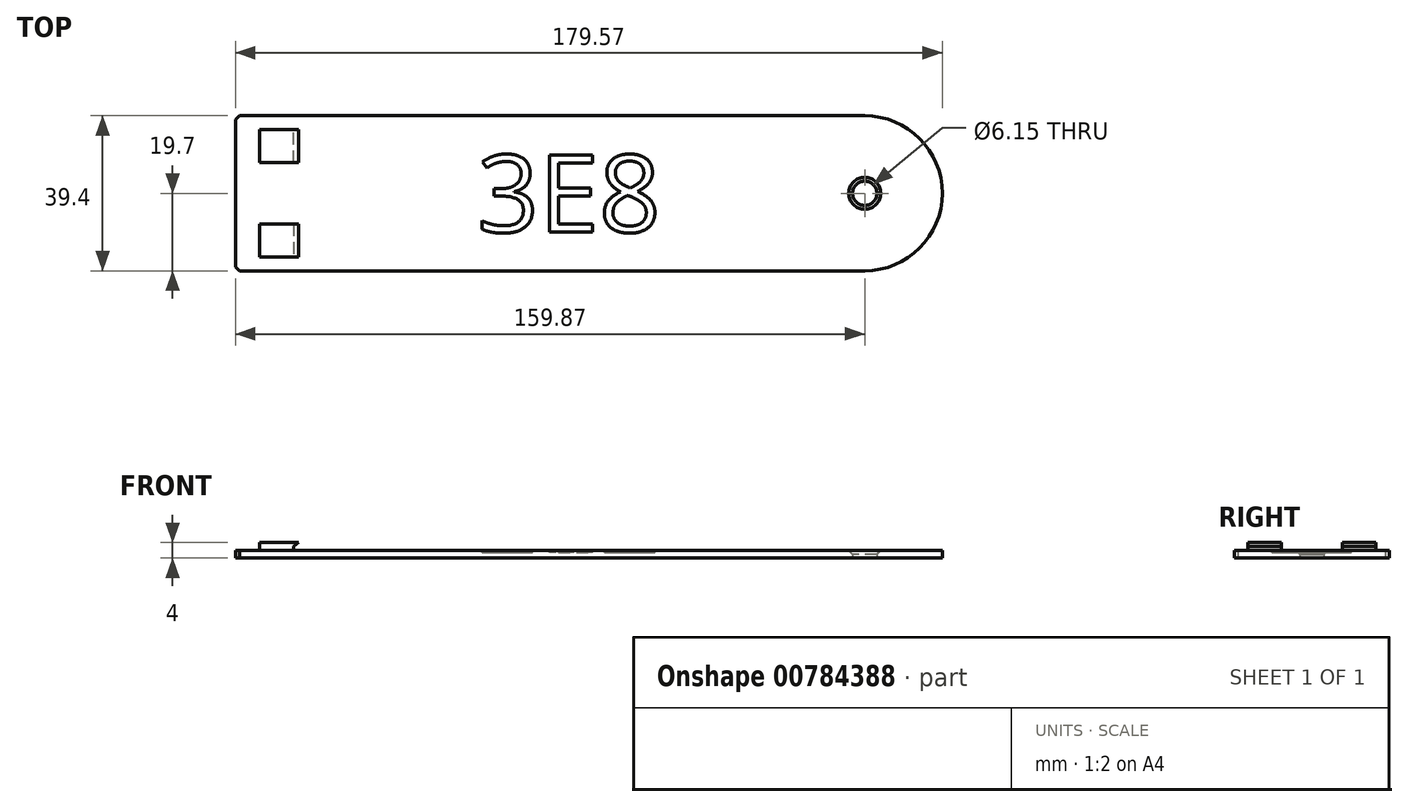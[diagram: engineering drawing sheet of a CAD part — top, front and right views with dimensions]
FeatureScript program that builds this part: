
annotation { "Feature Type Name" : "Feature", "Feature Type Description" : "" }
export const myFeature = defineFeature(function(context is Context, id is Id, definition is map)
    precondition{}
    {
        {
            assignVariable(context, id + "F0", {"name" : "slatthickness", "anyValue" : 2});
        }
        {
            var Q0;
            Q0=qCreatedBy(makeId("Top.planeOp"),FACE);
            var sketch = newSketch(context, id + "F1", { "sketchPlane" : qUnion([Q0])});
            skLineSegment(sketch, "E0", {"start": v(-75, 0) * mm, "end": v(75, 0) * mm, "construction": true});
            skLineSegment(sketch, "E1", {"start": v(-75, 12) * mm, "end": v(-75, -12) * mm, "construction": true});
            skLineSegment(sketch, "E2.bottom", {"start": v(-70.14, 7.8) * mm, "end": v(-79.86, 7.8) * mm, "construction": true});
            skLineSegment(sketch, "E2.top", {"start": v(-70.14, 16.2) * mm, "end": v(-79.86, 16.2) * mm, "construction": true});
            skLineSegment(sketch, "E2.left", {"start": v(-70.14, 7.8) * mm, "end": v(-70.14, 16.2) * mm, "construction": true});
            skLineSegment(sketch, "E2.right", {"start": v(-79.86, 7.8) * mm, "end": v(-79.86, 16.2) * mm, "construction": true});
            skPoint(sketch, "E2.middle", {"position": v(-75, 12) * mm});
            skLineSegment(sketch, "E3.MirrorCS", {"start": v(-70.14, -7.8) * mm, "end": v(-70.14, -16.2) * mm, "construction": true});
            skLineSegment(sketch, "E4.MirrorCS", {"start": v(-70.14, -16.2) * mm, "end": v(-79.86, -16.2) * mm, "construction": true});
            skLineSegment(sketch, "E5.MirrorCS", {"start": v(-79.86, -7.8) * mm, "end": v(-79.86, -16.2) * mm, "construction": true});
            skLineSegment(sketch, "E6.MirrorCS", {"start": v(-70.14, -7.8) * mm, "end": v(-79.86, -7.8) * mm, "construction": true});
            skCircle(sketch, "E7", {"center": v(75, 0) * mm, "radius": 3.08 * mm});
            skArc(sketch, "E8", {"start": v(75, -19.7) * mm, "mid": v(94.7, 0) * mm, "end": v(75, 19.7) * mm});
            skLineSegment(sketch, "E9", {"start": v(75, 19.7) * mm, "end": v(75, -19.7) * mm, "construction": true});
            skLineSegment(sketch, "E10", {"start": v(75, 19.7) * mm, "end": v(-84.87, 19.7) * mm});
            skLineSegment(sketch, "E11", {"start": v(-84.87, 19.7) * mm, "end": v(-84.87, -19.7) * mm});
            skLineSegment(sketch, "E12", {"start": v(-84.87, -19.7) * mm, "end": v(75, -19.7) * mm});
            skSolve(sketch);
        }
        {
            var Q0;
            Q0 = qSketchRegion(id + "F1", true);
            extrude(context, id + "F2", {"entities" : qUnion([Q0]), "depth" : (getVariable(context, 'slatthickness')) * mm, "offsetDistance" : 25 * mm});
        }
        {
            var Q0;
            Q0=makeQuery(id+"F2.opExtrude","CAP_FACE",FACE,{"disambiguationData":[OSD([sQuery(id+"F1.wireOp",EDGE,"E7"),sQuery(id+"F1.wireOp",EDGE,"E8"),sQuery(id+"F1.wireOp",EDGE,"E10"),sQuery(id+"F1.wireOp",EDGE,"E11"),sQuery(id+"F1.wireOp",EDGE,"E12")])],"isStart":false});
            var sketch = newSketch(context, id + "F3", { "sketchPlane" : qUnion([Q0])});
            skLineSegment(sketch, "E13.0", {"start": v(-70.14, 7.8) * mm, "end": v(-70.14, 16.2) * mm});
            skLineSegment(sketch, "E14.0", {"start": v(-70.14, 16.2) * mm, "end": v(-79.86, 16.2) * mm});
            skLineSegment(sketch, "E15.0", {"start": v(-79.86, 7.8) * mm, "end": v(-79.86, 16.2) * mm});
            skLineSegment(sketch, "E16.0", {"start": v(-70.14, 7.8) * mm, "end": v(-79.86, 7.8) * mm});
            skLineSegment(sketch, "E17.0", {"start": v(-70.14, -7.8) * mm, "end": v(-79.86, -7.8) * mm});
            skLineSegment(sketch, "E18.0", {"start": v(-79.86, -7.8) * mm, "end": v(-79.86, -16.2) * mm});
            skLineSegment(sketch, "E19.0", {"start": v(-70.14, -16.2) * mm, "end": v(-79.86, -16.2) * mm});
            skLineSegment(sketch, "E20.0", {"start": v(-70.14, -7.8) * mm, "end": v(-70.14, -16.2) * mm});
            skSolve(sketch);
        }
        {
            var Q0;
            Q0 = qSketchRegion(id + "F3", true);
            extrude(context, id + "F4", {"entities" : qUnion([Q0]), "operationType" : NewBodyOperationType.ADD, "depth" : (getVariable(context, 'slatthickness')) * mm, "offsetDistance" : 25 * mm});
        }
        {
            var Q0;
            Q0=makeQuery(id+"F2.opExtrude","CAP_EDGE",EDGE,{"disambiguationData":[OSD([sQuery(id+"F1.wireOp",EDGE,"E7")])],"isStart":false});
            var Q1;
            Q1=makeQuery(id+"F2.opExtrude","SWEPT_EDGE",EDGE,{"disambiguationData":[OSD([sQuery(id+"F1.wireOp",EDGE,"E11"),sQuery(id+"F1.wireOp",EDGE,"E12")])]});
            var Q2;
            Q2=makeQuery(id+"F2.opExtrude","SWEPT_EDGE",EDGE,{"disambiguationData":[OSD([sQuery(id+"F1.wireOp",EDGE,"E10"),sQuery(id+"F1.wireOp",EDGE,"E11")])]});
            chamfer(context, id + "F5", {"entities" : qUnion([Q0, Q1, Q2]), "width" : (getVariable(context, 'slatthickness') / 2) * mm, "tangentPropagation" : true});
        }
        {
            var Q0;
            Q0=makeQuery(id+"F4.opExtrude","SWEPT_FACE",FACE,{"disambiguationData":[OSD([sQuery(id+"F3.wireOp",EDGE,"E19.0")])]});
            var sketch = newSketch(context, id + "F6", { "sketchPlane" : qUnion([Q0])});
            skLineSegment(sketch, "E21", {"start": v(-70.14, 4) * mm, "end": v(-68.84, 4) * mm});
            skLineSegment(sketch, "E22", {"start": v(-68.84, 4) * mm, "end": v(-70.14, 3) * mm});
            skLineSegment(sketch, "E23", {"start": v(-70.14, 3) * mm, "end": v(-70.14, 4) * mm});
            skSolve(sketch);
        }
        {
            var Q0;
            Q0 = qSketchRegion(id + "F6", true);
            var Q1;
            Q1=makeQuery(id+"F4.opExtrude","SWEPT_FACE",FACE,{"disambiguationData":[OSD([sQuery(id+"F3.wireOp",EDGE,"E17.0")])]});
            extrude(context, id + "F7", {"entities" : qUnion([Q0]), "operationType" : NewBodyOperationType.ADD, "endBound" : BoundingType.UP_TO_SURFACE, "oppositeDirection" : true, "depth" : 25 * mm, "endBoundEntityFace" : qUnion([Q1]), "offsetDistance" : 25 * mm});
        }
        {
            var Q0;
            Q0=makeQuery(id+"F4.opExtrude","SWEPT_FACE",FACE,{"disambiguationData":[OSD([sQuery(id+"F3.wireOp",EDGE,"E16.0")])]});
            var sketch = newSketch(context, id + "F8", { "sketchPlane" : qUnion([Q0])});
            skLineSegment(sketch, "E24.0.0", {"start": v(-70.14, 3) * mm, "end": v(-68.84, 4) * mm});
            skLineSegment(sketch, "E24.0.1", {"start": v(-68.84, 4) * mm, "end": v(-70.14, 4) * mm});
            skLineSegment(sketch, "E24.0.2", {"start": v(-70.14, 4) * mm, "end": v(-70.14, 3) * mm});
            skSolve(sketch);
        }
        {
            var Q0;
            Q0 = qSketchRegion(id + "F8", true);
            var Q1;
            Q1=makeQuery(id+"F4.opExtrude","SWEPT_FACE",FACE,{"disambiguationData":[OSD([sQuery(id+"F3.wireOp",EDGE,"E14.0")])]});
            extrude(context, id + "F9", {"entities" : qUnion([Q0]), "operationType" : NewBodyOperationType.ADD, "endBound" : BoundingType.UP_TO_SURFACE, "oppositeDirection" : true, "depth" : 25 * mm, "endBoundEntityFace" : qUnion([Q1]), "offsetDistance" : 25 * mm});
        }
        {
            var Q0;
            Q0=makeQuery(id+"F2.opExtrude","CAP_FACE",FACE,{"disambiguationData":[OSD([sQuery(id+"F1.wireOp",EDGE,"E7"),sQuery(id+"F1.wireOp",EDGE,"E8"),sQuery(id+"F1.wireOp",EDGE,"E10"),sQuery(id+"F1.wireOp",EDGE,"E11"),sQuery(id+"F1.wireOp",EDGE,"E12")])],"isStart":false});
            var sketch = newSketch(context, id + "F10", { "sketchPlane" : qUnion([Q0])});
            skText(sketch, "E25", { "text": "3E8", "fontName": "OpenSans-Regular.ttf"});
            const initialGuessF10  = {"E25": [-0.02348, -0.00987, 1, 0, 0.01974]};
            skSetInitialGuess(sketch, initialGuessF10);
            skSolve(sketch);
        }
        {
            var Q0;
            Q0 = qSketchRegion(id + "F10", true);
            extrude(context, id + "F11", {"entities" : qUnion([Q0]), "operationType" : NewBodyOperationType.REMOVE, "oppositeDirection" : true, "depth" : .5 * mm, "offsetDistance" : 25 * mm});
        }
        {
            var Q0;
            Q0=makeQuery(id+"F9.boolean.opBoolean","MERGE",FACE,{"derivedFrom":[makeQuery(id+"F4.opExtrude","CAP_FACE",FACE,{"disambiguationData":[OSD([sQuery(id+"F3.wireOp",EDGE,"E13.0"),sQuery(id+"F3.wireOp",EDGE,"E14.0"),sQuery(id+"F3.wireOp",EDGE,"E15.0"),sQuery(id+"F3.wireOp",EDGE,"E16.0")])],"isStart":false}),makeQuery(id+"F9.opExtrude","SWEPT_FACE",FACE,{"disambiguationData":[OSD([sQuery(id+"F8.wireOp",EDGE,"E24.0.1")])]})]});
            var sketch = newSketch(context, id + "F12", { "sketchPlane" : qUnion([Q0])});
            skLineSegment(sketch, "E26.bottom", {"start": v(-79.86, 16.2) * mm, "end": v(-78.71, 16.2) * mm});
            skLineSegment(sketch, "E26.top", {"start": v(-79.86, 7.8) * mm, "end": v(-78.71, 7.8) * mm});
            skLineSegment(sketch, "E26.left", {"start": v(-79.86, 16.2) * mm, "end": v(-79.86, 7.8) * mm});
            skLineSegment(sketch, "E26.right", {"start": v(-78.71, 16.2) * mm, "end": v(-78.71, 7.8) * mm});
            skLineSegment(sketch, "E27.MirrorCS", {"start": v(-78.71, -16.2) * mm, "end": v(-78.71, -7.8) * mm});
            skLineSegment(sketch, "E28.MirrorCS", {"start": v(-79.86, -16.2) * mm, "end": v(-79.86, -7.8) * mm});
            skLineSegment(sketch, "E29.MirrorCS", {"start": v(-79.86, -7.8) * mm, "end": v(-78.71, -7.8) * mm});
            skLineSegment(sketch, "E30.MirrorCS", {"start": v(-79.86, -16.2) * mm, "end": v(-78.71, -16.2) * mm});
            skSolve(sketch);
        }
        {
            var Q0;
            Q0 = qSketchRegion(id + "F12", true);
            var Q1;
            {var subQ2=sQuery(id+"F1.wireOp",EDGE,"E11");var subQ3=sQuery(id+"F1.wireOp",EDGE,"E10");var subQ4=sQuery(id+"F1.wireOp",EDGE,"E8");var subQ5=sQuery(id+"F1.wireOp",EDGE,"E12");var subQ6=sQuery(id+"F1.wireOp",EDGE,"E7");Q1=makeQuery(id+"F11.boolean.opBoolean","SPLIT",FACE,{"disambiguationData":[TD([makeQuery(id+"F2.opExtrude","SWEPT_FACE",FACE,{"disambiguationData":[OSD([subQ4])]})])],"derivedFrom":makeQuery(id+"F2.opExtrude","CAP_FACE",FACE,{"disambiguationData":[OSD([subQ6,subQ4,subQ3,subQ2,subQ5])],"isStart":false})});}
            extrude(context, id + "F13", {"entities" : qUnion([Q0]), "operationType" : NewBodyOperationType.REMOVE, "endBound" : BoundingType.UP_TO_SURFACE, "oppositeDirection" : true, "depth" : 25 * mm, "endBoundEntityFace" : qUnion([Q1]), "offsetDistance" : 25 * mm});
        }
    });
